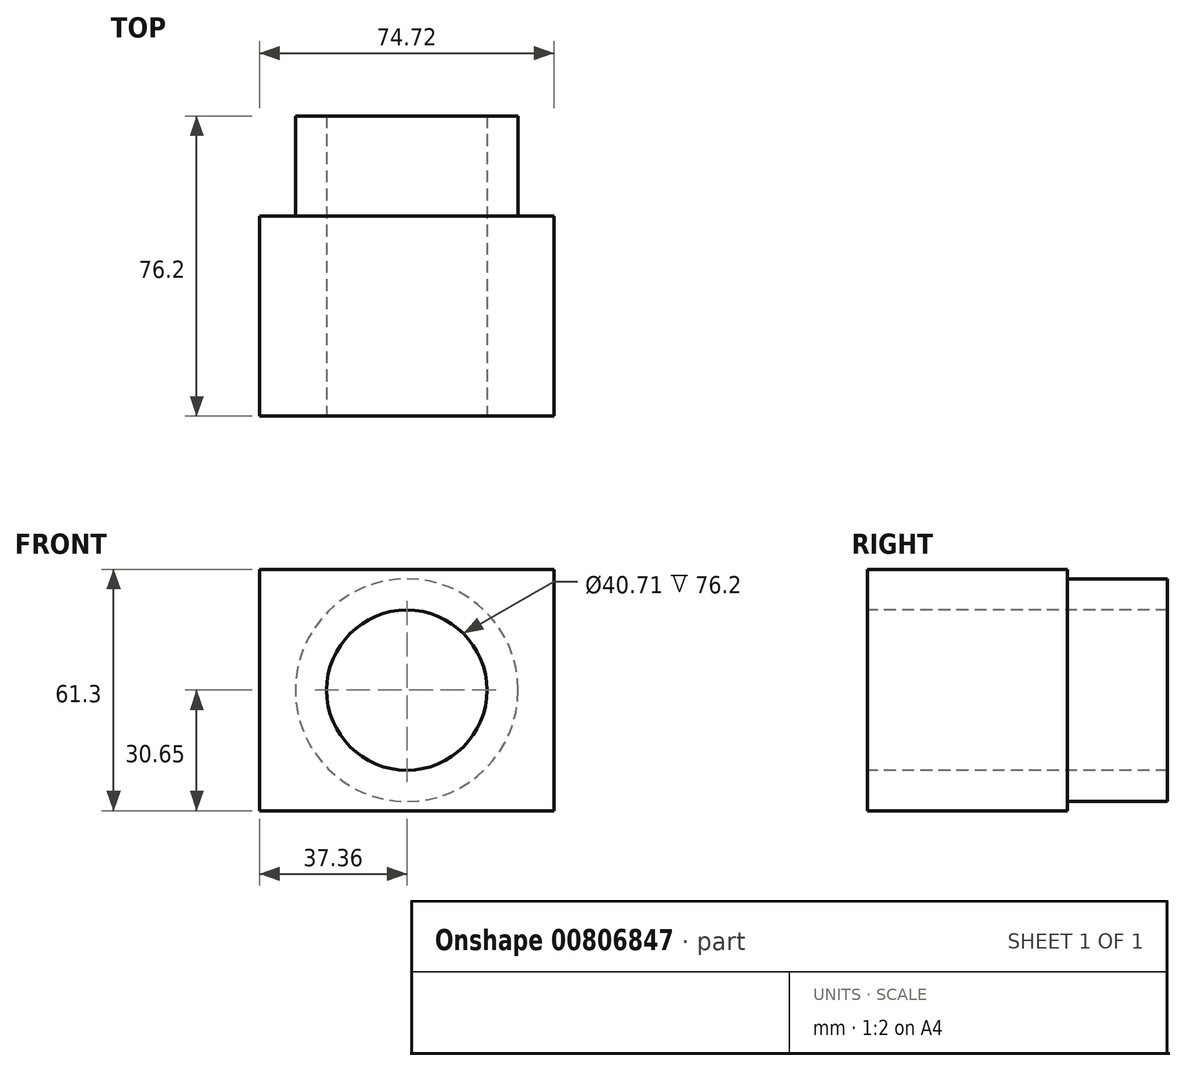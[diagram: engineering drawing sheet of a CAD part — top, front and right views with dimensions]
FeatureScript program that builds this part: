
annotation { "Feature Type Name" : "Feature", "Feature Type Description" : "" }
export const myFeature = defineFeature(function(context is Context, id is Id, definition is map)
    precondition{}
    {
        {
            var Q0;
            Q0=qCreatedBy(makeId("Front.planeOp"),FACE);
            var sketch = newSketch(context, id + "F0", { "sketchPlane" : qUnion([Q0])});
            skLineSegment(sketch, "E0.bottom", {"start": v(-37.36, 30.65) * mm, "end": v(37.36, 30.65) * mm});
            skLineSegment(sketch, "E0.top", {"start": v(-37.36, -30.65) * mm, "end": v(37.36, -30.65) * mm});
            skLineSegment(sketch, "E0.left", {"start": v(-37.36, 30.65) * mm, "end": v(-37.36, -30.65) * mm});
            skLineSegment(sketch, "E0.right", {"start": v(37.36, 30.65) * mm, "end": v(37.36, -30.65) * mm});
            skPoint(sketch, "E0.middle", {"position": v(0, 0) * mm});
            skSolve(sketch);
        }
        {
            var Q0;
            Q0 = qSketchRegion(id + "F0", true);
            extrude(context, id + "F1", {"entities" : qUnion([Q0]), "endBound" : BoundingType.SYMMETRIC, "depth" : 50.8 * mm, "offsetDistance" : 25.4 * mm});
        }
        {
            var Q0;
            Q0=makeQuery(id+"F1.opExtrude","CAP_FACE",FACE,{"disambiguationData":[OSD([sQuery(id+"F0.wireOp",EDGE,"E0.bottom"),sQuery(id+"F0.wireOp",EDGE,"E0.top"),sQuery(id+"F0.wireOp",EDGE,"E0.left"),sQuery(id+"F0.wireOp",EDGE,"E0.right")])],"isStart":false});
            var sketch = newSketch(context, id + "F2", { "sketchPlane" : qUnion([Q0])});
            skCircle(sketch, "E1", {"center": v(0, 0) * mm, "radius": 20.35 * mm});
            skCircle(sketch, "E2", {"center": v(0, 0) * mm, "radius": 26.8 * mm});
            skSolve(sketch);
        }
        {
            var Q0;
            Q0=makeQuery(id+"F2.imprint","IMPRINT",FACE,{"disambiguationData":[TD([[makeQuery(id+"F2.imprint","IMPRINT",EDGE,{"derivedFrom":sQuery(id+"F2.wireOp",EDGE,"E1")}),1.0]])]});
            extrude(context, id + "F3", {"entities" : qUnion([Q0]), "operationType" : NewBodyOperationType.REMOVE, "endBound" : BoundingType.THROUGH_ALL, "oppositeDirection" : true, "depth" : 25.4 * mm, "offsetDistance" : 25.4 * mm});
        }
        {
            var Q0;
            Q0=makeQuery(id+"F1.opExtrude","CAP_FACE",FACE,{"disambiguationData":[OSD([sQuery(id+"F0.wireOp",EDGE,"E0.bottom"),sQuery(id+"F0.wireOp",EDGE,"E0.top"),sQuery(id+"F0.wireOp",EDGE,"E0.left"),sQuery(id+"F0.wireOp",EDGE,"E0.right")])],"isStart":true});
            var sketch = newSketch(context, id + "F4", { "sketchPlane" : qUnion([Q0])});
            skCircle(sketch, "E3", {"center": v(0, 0) * mm, "radius": 28.28 * mm});
            skSolve(sketch);
        }
        {
            var Q0;
            Q0=makeQuery(id+"F4.imprint","IMPRINT",FACE,{"disambiguationData":[TD([[makeQuery(id+"F4.imprint","IMPRINT",EDGE,{"derivedFrom":sQuery(id+"F4.wireOp",EDGE,"E3")}),1.0]])]});
            extrude(context, id + "F5", {"entities" : qUnion([Q0]), "operationType" : NewBodyOperationType.ADD, "depth" : 25.4 * mm, "offsetDistance" : 25.4 * mm});
        }
    });
